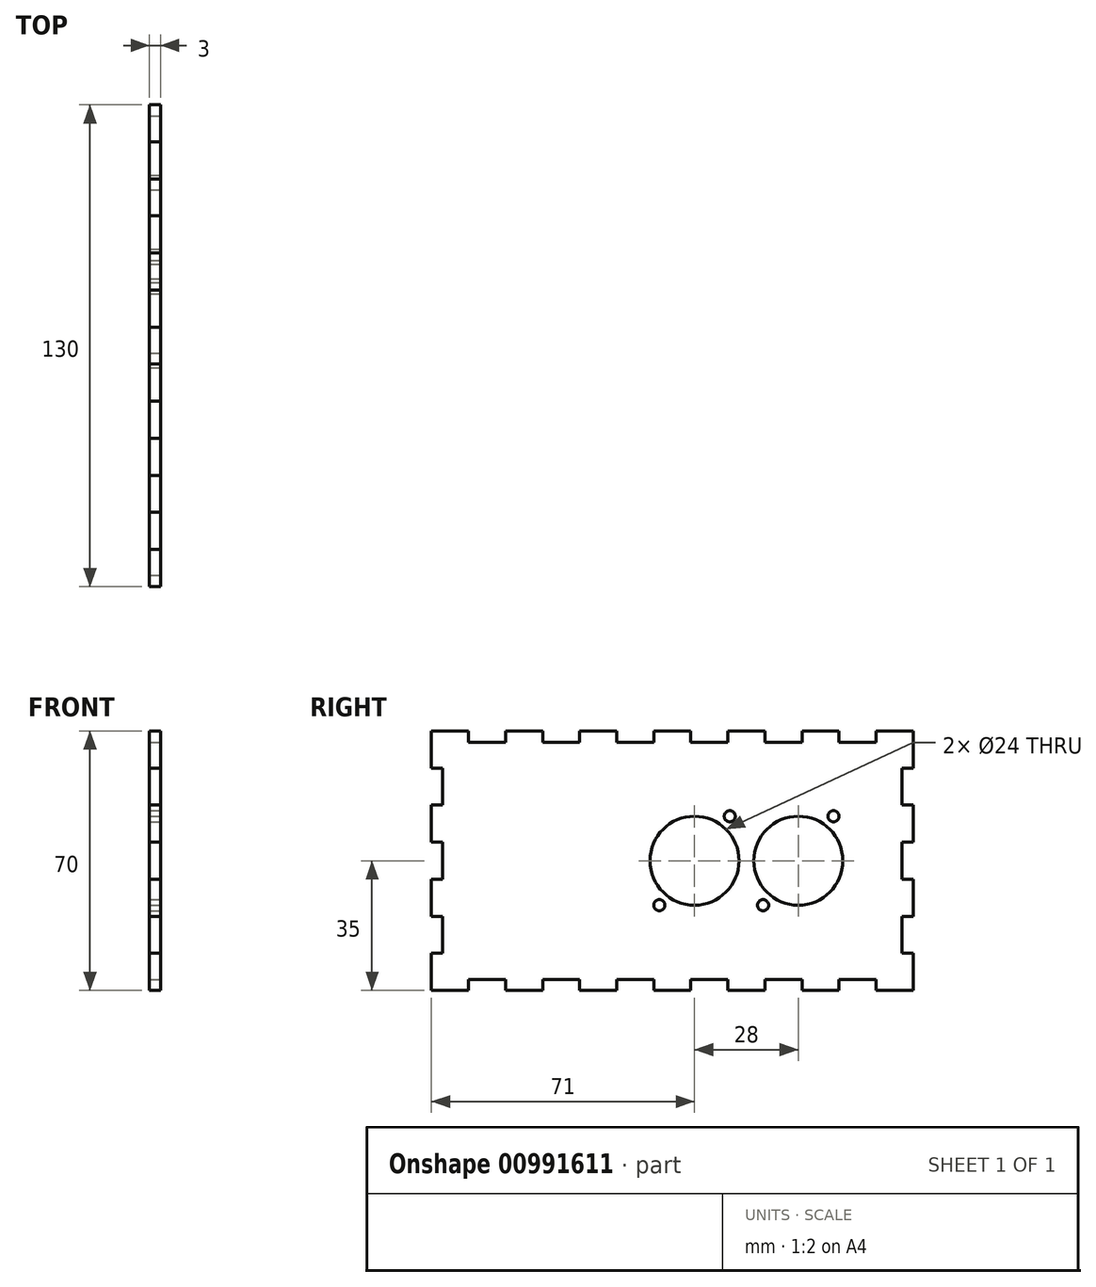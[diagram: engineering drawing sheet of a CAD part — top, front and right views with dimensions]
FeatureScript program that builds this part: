
annotation { "Feature Type Name" : "Feature", "Feature Type Description" : "" }
export const myFeature = defineFeature(function(context is Context, id is Id, definition is map)
    precondition{}
    {
        {
            var Q0;
            Q0=qCreatedBy(makeId("Right.planeOp"),FACE);
            var sketch = newSketch(context, id + "F0", { "sketchPlane" : qUnion([Q0])});
            skLineSegment(sketch, "E0.bottom", {"start": v(65, -35) * mm, "end": v(-65, -35) * mm});
            skLineSegment(sketch, "E0.top", {"start": v(65, 35) * mm, "end": v(-65, 35) * mm});
            skLineSegment(sketch, "E0.left", {"start": v(65, -35) * mm, "end": v(65, 35) * mm});
            skLineSegment(sketch, "E0.right", {"start": v(-65, -35) * mm, "end": v(-65, 35) * mm});
            skPoint(sketch, "E0.middle", {"position": v(0, 0) * mm});
            skSolve(sketch);
        }
        {
            var Q0;
            Q0=qSketchRegion(id+"F0",true);
            extrude(context, id + "F1", {"entities" : qUnion([Q0]), "depth" : 3 * mm, "offsetDistance" : 25 * mm});
        }
        {
            var Q0;
            Q0=makeQuery(id+"F1.opExtrude","CAP_FACE",FACE,{"disambiguationData":[OSD([sQuery(id+"F0.wireOp",EDGE,"E0.bottom"),sQuery(id+"F0.wireOp",EDGE,"E0.top"),sQuery(id+"F0.wireOp",EDGE,"E0.left"),sQuery(id+"F0.wireOp",EDGE,"E0.right")])],"isStart":false});
            var sketch = newSketch(context, id + "F2", { "sketchPlane" : qUnion([Q0])});
            skLineSegment(sketch, "E1.bottom", {"start": v(-65, 25) * mm, "end": v(-62, 25) * mm});
            skLineSegment(sketch, "E1.top", {"start": v(-65, 15) * mm, "end": v(-62, 15) * mm});
            skLineSegment(sketch, "E1.left", {"start": v(-65, 25) * mm, "end": v(-65, 15) * mm});
            skLineSegment(sketch, "E1.right", {"start": v(-62, 25) * mm, "end": v(-62, 15) * mm});
            skLineSegment(sketch, "E2.0.1.0", {"start": v(-65, 5) * mm, "end": v(-65, -5) * mm});
            skLineSegment(sketch, "E2.0.1.1", {"start": v(-65, 5) * mm, "end": v(-62, 5) * mm});
            skLineSegment(sketch, "E2.0.1.2", {"start": v(-62, 5) * mm, "end": v(-62, -5) * mm});
            skLineSegment(sketch, "E2.0.1.3", {"start": v(-65, -5) * mm, "end": v(-62, -5) * mm});
            skLineSegment(sketch, "E2.0.2.0", {"start": v(-65, -15) * mm, "end": v(-65, -25) * mm});
            skLineSegment(sketch, "E2.0.2.1", {"start": v(-65, -15) * mm, "end": v(-62, -15) * mm});
            skLineSegment(sketch, "E2.0.2.2", {"start": v(-62, -15) * mm, "end": v(-62, -25) * mm});
            skLineSegment(sketch, "E2.0.2.3", {"start": v(-65, -25) * mm, "end": v(-62, -25) * mm});
            skLineSegment(sketch, "E2.direction1", {"start": v(-65, 15) * mm, "end": v(-35, 15) * mm, "construction": true});
            skLineSegment(sketch, "E2.direction2", {"start": v(-65, 15) * mm, "end": v(-65, -5) * mm, "construction": true});
            skLineSegment(sketch, "E3", {"start": v(0, 35) * mm, "end": v(0, -35) * mm, "construction": true});
            skLineSegment(sketch, "E4.MirrorCS", {"start": v(65, 5) * mm, "end": v(65, -5) * mm});
            skLineSegment(sketch, "E5.MirrorCS", {"start": v(62, 5) * mm, "end": v(62, -5) * mm});
            skLineSegment(sketch, "E6.MirrorCS", {"start": v(65, -5) * mm, "end": v(62, -5) * mm});
            skLineSegment(sketch, "E7.MirrorCS", {"start": v(65, 15) * mm, "end": v(65, -5) * mm, "construction": true});
            skLineSegment(sketch, "E8.MirrorCS", {"start": v(65, 25) * mm, "end": v(62, 25) * mm});
            skLineSegment(sketch, "E9.MirrorCS", {"start": v(65, -15) * mm, "end": v(65, -25) * mm});
            skLineSegment(sketch, "E10.MirrorCS", {"start": v(65, 15) * mm, "end": v(62, 15) * mm});
            skLineSegment(sketch, "E11.MirrorCS", {"start": v(62, -15) * mm, "end": v(62, -25) * mm});
            skLineSegment(sketch, "E12.MirrorCS", {"start": v(62, 25) * mm, "end": v(62, 15) * mm});
            skLineSegment(sketch, "E13.MirrorCS", {"start": v(65, -25) * mm, "end": v(62, -25) * mm});
            skLineSegment(sketch, "E14.MirrorCS", {"start": v(65, -15) * mm, "end": v(62, -15) * mm});
            skLineSegment(sketch, "E15.MirrorCS", {"start": v(65, 25) * mm, "end": v(65, 15) * mm});
            skLineSegment(sketch, "E16.MirrorCS", {"start": v(65, 5) * mm, "end": v(62, 5) * mm});
            skLineSegment(sketch, "E17", {"start": v(-65, 0) * mm, "end": v(65, 0) * mm, "construction": true});
            skLineSegment(sketch, "E18.bottom", {"start": v(-55, -35) * mm, "end": v(-45, -35) * mm});
            skLineSegment(sketch, "E18.top", {"start": v(-55, -32) * mm, "end": v(-45, -32) * mm});
            skLineSegment(sketch, "E18.left", {"start": v(-55, -35) * mm, "end": v(-55, -32) * mm});
            skLineSegment(sketch, "E18.right", {"start": v(-45, -35) * mm, "end": v(-45, -32) * mm});
            skLineSegment(sketch, "E19.1.0.0", {"start": v(-35, -35) * mm, "end": v(-35, -32) * mm});
            skLineSegment(sketch, "E19.1.0.1", {"start": v(-35, -32) * mm, "end": v(-25, -32) * mm});
            skLineSegment(sketch, "E19.1.0.2", {"start": v(-25, -35) * mm, "end": v(-25, -32) * mm});
            skLineSegment(sketch, "E19.1.0.3", {"start": v(-35, -35) * mm, "end": v(-25, -35) * mm});
            skLineSegment(sketch, "E19.2.0.0", {"start": v(-15, -35) * mm, "end": v(-15, -32) * mm});
            skLineSegment(sketch, "E19.2.0.1", {"start": v(-15, -32) * mm, "end": v(-5, -32) * mm});
            skLineSegment(sketch, "E19.2.0.2", {"start": v(-5, -35) * mm, "end": v(-5, -32) * mm});
            skLineSegment(sketch, "E19.2.0.3", {"start": v(-15, -35) * mm, "end": v(-5, -35) * mm});
            skLineSegment(sketch, "E19.3.0.0", {"start": v(5, -35) * mm, "end": v(5, -32) * mm});
            skLineSegment(sketch, "E19.3.0.1", {"start": v(5, -32) * mm, "end": v(15, -32) * mm});
            skLineSegment(sketch, "E19.3.0.2", {"start": v(15, -35) * mm, "end": v(15, -32) * mm});
            skLineSegment(sketch, "E19.3.0.3", {"start": v(5, -35) * mm, "end": v(15, -35) * mm});
            skLineSegment(sketch, "E19.4.0.0", {"start": v(25, -35) * mm, "end": v(25, -32) * mm});
            skLineSegment(sketch, "E19.4.0.1", {"start": v(25, -32) * mm, "end": v(35, -32) * mm});
            skLineSegment(sketch, "E19.4.0.2", {"start": v(35, -35) * mm, "end": v(35, -32) * mm});
            skLineSegment(sketch, "E19.4.0.3", {"start": v(25, -35) * mm, "end": v(35, -35) * mm});
            skLineSegment(sketch, "E19.5.0.0", {"start": v(45, -35) * mm, "end": v(45, -32) * mm});
            skLineSegment(sketch, "E19.5.0.1", {"start": v(45, -32) * mm, "end": v(55, -32) * mm});
            skLineSegment(sketch, "E19.5.0.2", {"start": v(55, -35) * mm, "end": v(55, -32) * mm});
            skLineSegment(sketch, "E19.5.0.3", {"start": v(45, -35) * mm, "end": v(55, -35) * mm});
            skLineSegment(sketch, "E19.direction1", {"start": v(-55, -35) * mm, "end": v(-35, -35) * mm, "construction": true});
            skLineSegment(sketch, "E20.MirrorCS", {"start": v(-55, 35) * mm, "end": v(-45, 35) * mm});
            skLineSegment(sketch, "E21.MirrorCS", {"start": v(-25, 35) * mm, "end": v(-25, 32) * mm});
            skLineSegment(sketch, "E22.MirrorCS", {"start": v(45, 32) * mm, "end": v(55, 32) * mm});
            skLineSegment(sketch, "E23.MirrorCS", {"start": v(45, 35) * mm, "end": v(55, 35) * mm});
            skLineSegment(sketch, "E24.MirrorCS", {"start": v(-35, 35) * mm, "end": v(-25, 35) * mm});
            skLineSegment(sketch, "E25.MirrorCS", {"start": v(-35, 32) * mm, "end": v(-25, 32) * mm});
            skLineSegment(sketch, "E26.MirrorCS", {"start": v(-5, 35) * mm, "end": v(-5, 32) * mm});
            skLineSegment(sketch, "E27.MirrorCS", {"start": v(-55, 35) * mm, "end": v(-55, 32) * mm});
            skLineSegment(sketch, "E28.MirrorCS", {"start": v(5, 32) * mm, "end": v(15, 32) * mm});
            skLineSegment(sketch, "E29.MirrorCS", {"start": v(55, 35) * mm, "end": v(55, 32) * mm});
            skLineSegment(sketch, "E30.MirrorCS", {"start": v(5, 35) * mm, "end": v(15, 35) * mm});
            skLineSegment(sketch, "E31.MirrorCS", {"start": v(-15, 32) * mm, "end": v(-5, 32) * mm});
            skLineSegment(sketch, "E32.MirrorCS", {"start": v(5, 35) * mm, "end": v(5, 32) * mm});
            skLineSegment(sketch, "E33.MirrorCS", {"start": v(-55, 32) * mm, "end": v(-45, 32) * mm});
            skLineSegment(sketch, "E34.MirrorCS", {"start": v(-55, 35) * mm, "end": v(-35, 35) * mm, "construction": true});
            skLineSegment(sketch, "E35.MirrorCS", {"start": v(35, 35) * mm, "end": v(35, 32) * mm});
            skLineSegment(sketch, "E36.MirrorCS", {"start": v(25, 35) * mm, "end": v(25, 32) * mm});
            skLineSegment(sketch, "E37.MirrorCS", {"start": v(-15, 35) * mm, "end": v(-5, 35) * mm});
            skLineSegment(sketch, "E38.MirrorCS", {"start": v(15, 35) * mm, "end": v(15, 32) * mm});
            skLineSegment(sketch, "E39.MirrorCS", {"start": v(25, 32) * mm, "end": v(35, 32) * mm});
            skLineSegment(sketch, "E40.MirrorCS", {"start": v(-15, 35) * mm, "end": v(-15, 32) * mm});
            skLineSegment(sketch, "E41.MirrorCS", {"start": v(45, 35) * mm, "end": v(45, 32) * mm});
            skLineSegment(sketch, "E42.MirrorCS", {"start": v(-35, 35) * mm, "end": v(-35, 32) * mm});
            skLineSegment(sketch, "E43.MirrorCS", {"start": v(25, 35) * mm, "end": v(35, 35) * mm});
            skLineSegment(sketch, "E44.MirrorCS", {"start": v(-45, 35) * mm, "end": v(-45, 32) * mm});
            skSolve(sketch);
        }
        {
            var Q0;
            Q0=qSketchRegion(id+"F2",true);
            extrude(context, id + "F3", {"entities" : qUnion([Q0]), "operationType" : NewBodyOperationType.REMOVE, "endBound" : BoundingType.THROUGH_ALL, "oppositeDirection" : true, "depth" : 25 * mm, "offsetDistance" : 25 * mm});
        }
        {
            var Q0;
            Q0=makeQuery(id+"F1.opExtrude","CAP_FACE",FACE,{"disambiguationData":[OSD([sQuery(id+"F0.wireOp",EDGE,"E0.bottom"),sQuery(id+"F0.wireOp",EDGE,"E0.top"),sQuery(id+"F0.wireOp",EDGE,"E0.left"),sQuery(id+"F0.wireOp",EDGE,"E0.right")])],"isStart":false});
            var sketch = newSketch(context, id + "F4", { "sketchPlane" : qUnion([Q0])});
            skLineSegment(sketch, "E45.bottom", {"start": v(47, 15.5) * mm, "end": v(21, 15.5) * mm, "construction": true});
            skLineSegment(sketch, "E45.top", {"start": v(47, -15.5) * mm, "end": v(21, -15.5) * mm, "construction": true});
            skLineSegment(sketch, "E45.left", {"start": v(47, 15.5) * mm, "end": v(47, -15.5) * mm, "construction": true});
            skLineSegment(sketch, "E45.right", {"start": v(21, 15.5) * mm, "end": v(21, -15.5) * mm, "construction": true});
            skLineSegment(sketch, "E46", {"start": v(47, 15.5) * mm, "end": v(21, -15.5) * mm, "construction": true});
            skCircle(sketch, "E47", {"center": v(34, 0) * mm, "radius": 12 * mm});
            skLineSegment(sketch, "E48.bottom", {"start": v(24.5, 12) * mm, "end": v(43.5, 12) * mm, "construction": true});
            skLineSegment(sketch, "E48.top", {"start": v(24.5, -12) * mm, "end": v(43.5, -12) * mm, "construction": true});
            skLineSegment(sketch, "E48.left", {"start": v(24.5, 12) * mm, "end": v(24.5, -12) * mm, "construction": true});
            skLineSegment(sketch, "E48.right", {"start": v(43.5, 12) * mm, "end": v(43.5, -12) * mm, "construction": true});
            skCircle(sketch, "E49", {"center": v(43.5, 12) * mm, "radius": 1.5 * mm});
            skCircle(sketch, "E50", {"center": v(24.5, -12) * mm, "radius": 1.5 * mm});
            skLineSegment(sketch, "E51", {"start": v(62, 0) * mm, "end": v(-62, 0) * mm, "construction": true});
            skCircle(sketch, "E52.1.0.0", {"center": v(6, 0) * mm, "radius": 12 * mm});
            skCircle(sketch, "E52.1.0.1", {"center": v(-3.5, -12) * mm, "radius": 1.5 * mm});
            skCircle(sketch, "E52.1.0.2", {"center": v(15.5, 12) * mm, "radius": 1.5 * mm});
            skLineSegment(sketch, "E52.1.0.3", {"start": v(-7, 15.5) * mm, "end": v(-7, -15.5) * mm, "construction": true});
            skLineSegment(sketch, "E52.1.0.4", {"start": v(19, 15.5) * mm, "end": v(19, -15.5) * mm, "construction": true});
            skLineSegment(sketch, "E52.1.0.5", {"start": v(19, 15.5) * mm, "end": v(-7, 15.5) * mm, "construction": true});
            skLineSegment(sketch, "E52.1.0.6", {"start": v(19, -15.5) * mm, "end": v(-7, -15.5) * mm, "construction": true});
            skLineSegment(sketch, "E52.direction1", {"start": v(24.5, -12) * mm, "end": v(-3.5, -12) * mm, "construction": true});
            skSolve(sketch);
        }
        {
            var Q0;
            Q0=qSketchRegion(id+"F4",true);
            extrude(context, id + "F5", {"entities" : qUnion([Q0]), "operationType" : NewBodyOperationType.REMOVE, "endBound" : BoundingType.THROUGH_ALL, "oppositeDirection" : true, "depth" : 25 * mm, "offsetDistance" : 25 * mm});
        }
    });
